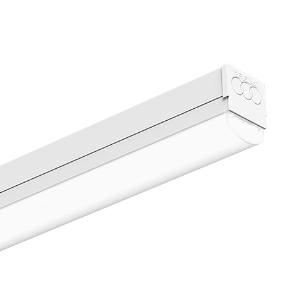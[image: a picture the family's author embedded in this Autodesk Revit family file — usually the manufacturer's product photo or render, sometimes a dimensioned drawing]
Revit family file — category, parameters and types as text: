
# Revit family: 3f_filippi_-_3f_zeta_d_3f_filippi_-_10874_-_3f_zeta_d_2x18_led_l1194
name_source: partatom
category: Lighting Fixtures
units: mm (PartAtom-declared; Revit-internal decimal feet)

## family parameters
Cut with Voids When Loaded = No
Host = Face
Light Source = No
Part Type = Normal
Room Calculation Point = No
Round Connector Dimension = Use Diameter
Shared = No

## types (1)
- 3F Filippi - 3F Zeta D (1 x LED, 4838 lm, 40 W, 4000 K)
    Apparent Load = 40 VA
    Approval mark = CE
    CIE Flux Codes = 42 71 90 91 100
    Color Rendering = 80
    Color Temperature = 4000 K
    Control Gear = Electronic ballast
    Default Elevation = 1800 mm
    Description = ILLUMINOTECHNICAL
Luminous efficiency 100% (DLOR 91%, ULOR 9%).
Initial luminous flux of the luminaire 4838 lm.
Diffused symmetric distribution.
Installation Interdistance Transv.D = 1.31 x hu - Long.D = 1.25 x hu.
Tabular UGR (CIE 117 - 4H-8H; S=0.25H; 70/50/20): RUG 26.1 - 24.4.
Beam angle: 130° - 112°.
Luminous efficacy 121 lm/W.
Lifetime (L93/B10): 30000 h. (tq+25°C)
Lifetime (L90/B10): 50000 h. (tq+25°C)
Lifetime (L85/B10): 80000 h. (tq+25°C)
Lifetime (L80/B10): 100000 h. (tq+25°C)
Sudden decreased luminous flux after 50000 hours: 0% (C0).
Photobiological safety in compliance with IEC/TR 62778: RG0 risk exempt, (IEC 62471).
In compliance with IEC/EN 62722-2-1 - IEC/EN 62717 standards.

SOURCE
2 linear LED modules 18W/840.
Energy efficiency class (UE 2019/2020 - UE 2019/2015): D.
CIE 13.3 Colour rendering index: CRI >80 (R9 <50%).
IES TM-30 Fidelity Index: Rf = 84 Rg = 95.
CCT nominal colour temperature 4000 K.
Colour initial tolerance (MacAdam): SDCM 3.

MECHANICAL
Housing in hot-galvanised steel, painted in white polyester, obtained through rolling process.
Light unit in hot-galvanised steel, painted in white polyester base with fixing springs and retractable safety hooks in stainless steel.
Curved screen in self-extinguishing polycarbonate, UV stabilised, opal, with smooth outer surface.
End caps in white polycarbonate.
Pair of stainless steel sliding brackets with sliding block screws.
Luminaire with limited surface temperature. - D - (EN 60598-2-24)
Dimensions: 1194x62 mm, height 81 mm. Weight 2.92 kg.
IP40 protection degree.
Mechanical strength to impacts IK06 (1 joule).
Glow-wire test resistance 850°C.

ELECTRICAL
Halogen Free electronic wiring 230V-50/60Hz, power factor 0.95, THD <25%, constant output current, SELV, class I, 1 driver.
Power of the luminaire 40 W.
ENEC - CE.
SAFE FLICKER: PstLM=<1 and SVM=<0.4 (IEC TR 61547-1 and IEC TR 63158), to ensure a more comfortable and safe light.
Luminaire compliant with EN 60598-2-22 for power supply from a centralised emergency system CPSS (Central Power Supply System), not incorporated in the luminaire - high risk areas excluded. The default power and flux are 100% in AC and 100% in DC.
Ambient temperature from 0°C to +25°C.
Temperature class T6 max 85°C.
Relative humidity UR: <85%.

INSTALLATION
Ceiling / Suspended / Wall.
All accessories dedicated to this product are available on the Catalog and on our website www.3F-Filippi.com.

APPLICATIONS
Suitable product for food production plants (HACCP), IFS (Food Version 6), BRC (GSFS Food Version 7).
In commercial environments, exhibition areas, shops and stores.

WARNING
Luminaire designed for disposal/recycling at end-of-life.
Replaceable (LED only) light source by a professional. Replaceable control gear by a professional.
    Height = 81 mm
    Lamp = 1 x LED
    Lamp Light Flux = 4838 lm
    Lamp Power = 40 W
    Lamp count = 1
    Length = 1194 mm
    Lifetime = 50000 h
    Luminous efficacy = 121 lm/W
    Manufacturer = 3F Filippi
    ModVariant = No
    Model = 3F Filippi - 10874 - 3F Zeta D 2x18 LED L1194
    Mounting Place = Ceiling
    Mounting Type = Pendant
    Number of Poles = 1
    OnlyDefault = Yes
    Power Factor = 1
    Product Name = 3F Filippi - 3F Zeta D
    Product group = pendant luminaire
    ProductGroupID = 9
    Protection Class = Protection class I
    Protection Degree = IP 40
    RLX_Detail_Level = 1
    RLX_Emergency_Light_Flux = 0 lm
    RLX_Emergency_Type = 0
    RLX_Emergency_Type_DB = No
    RlxData = <blob elided: 33341 chars, md5=68b852ab>
    Socket = socket
    Standby Power = 0 W
    System Light Flux = 4838 lm
    System Power = 40 W
    Type Comments = Product without accessories
    Type Image = 3ffilippi_3f_zeta_d.jpg
    URL = http://relux.com
    VarID = ---
    Voltage = 0 V
    Weight = 0.00 kg
    Width = 62 mm  [stored 0.203412 ft]

note: [stored X ft] marks values corroborated as IEEE doubles in the binary element streams (Revit-internal decimal feet)

## geometry (parser evidence)
native form markers: Blend x4, Sweep x13
no freeform markers — native parametric forms only
